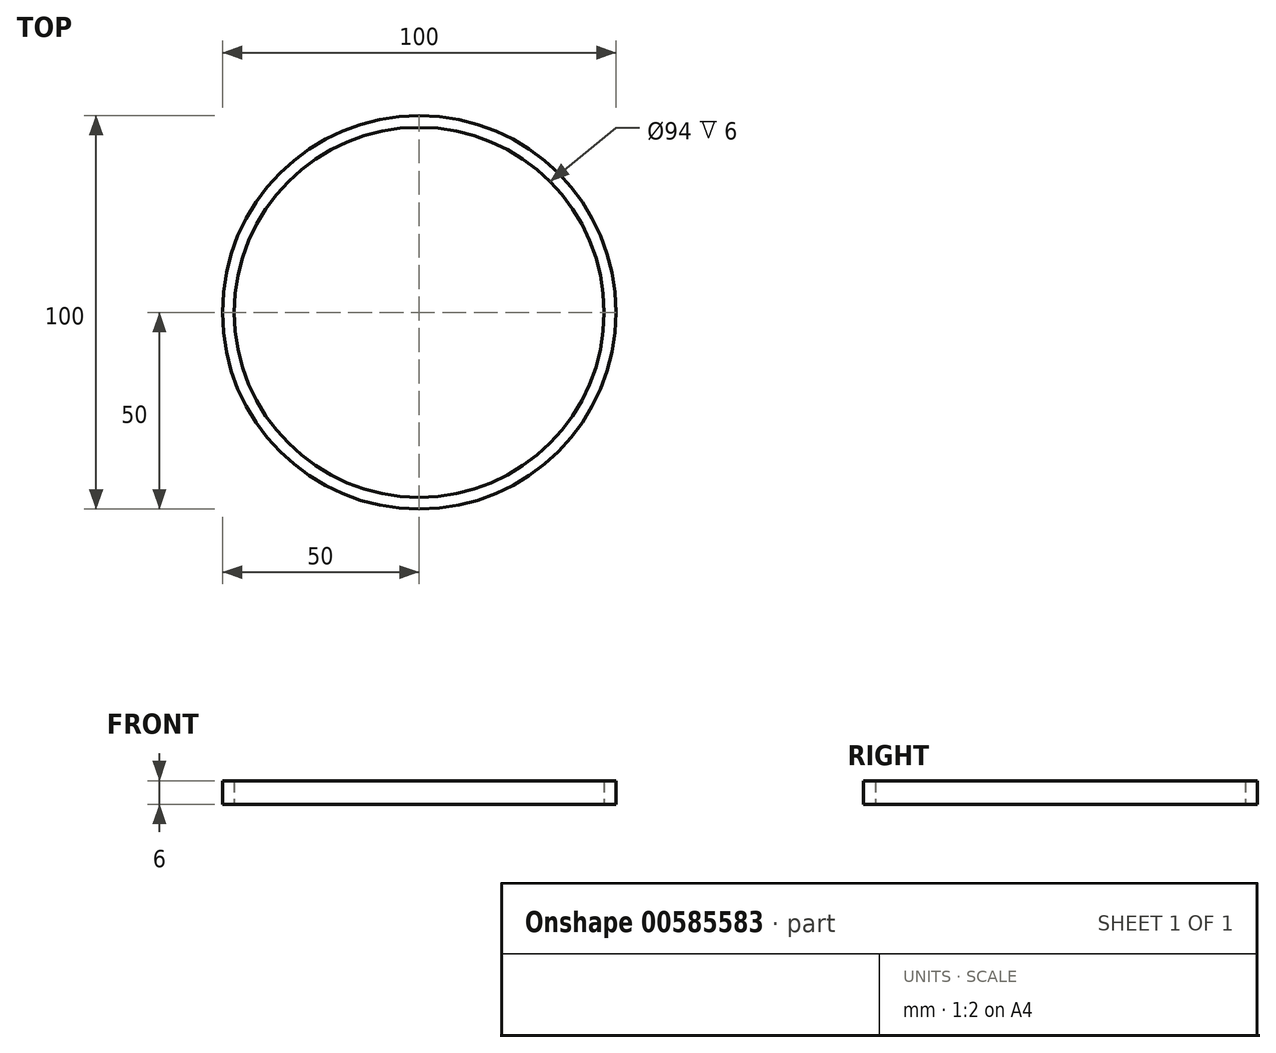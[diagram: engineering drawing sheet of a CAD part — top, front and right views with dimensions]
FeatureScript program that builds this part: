
annotation { "Feature Type Name" : "Feature", "Feature Type Description" : "" }
export const myFeature = defineFeature(function(context is Context, id is Id, definition is map)
    precondition{}
    {
        {
            var Q0;
            Q0=qCreatedBy(makeId("Top.planeOp"),FACE);
            var sketch = newSketch(context, id + "F0", { "sketchPlane" : qUnion([Q0])});
            skCircle(sketch, "E0", {"center": v(0, 0) * mm, "radius": 47 * mm});
            skCircle(sketch, "E1.0", {"center": v(0, 0) * mm, "radius": 50 * mm});
            skLineSegment(sketch, "E2", {"start": v(0, 47) * mm, "end": v(0, -47) * mm, "construction": true});
            skLineSegment(sketch, "E3", {"start": v(-47, 0) * mm, "end": v(47, 0) * mm, "construction": true});
            skSolve(sketch);
        }
        {
            var Q0;
            Q0 = qSketchRegion(id + "F0", true);
            extrude(context, id + "F1", {"entities" : qUnion([Q0]), "depth" : 6 * mm, "offsetDistance" : 25 * mm});
        }
    });
